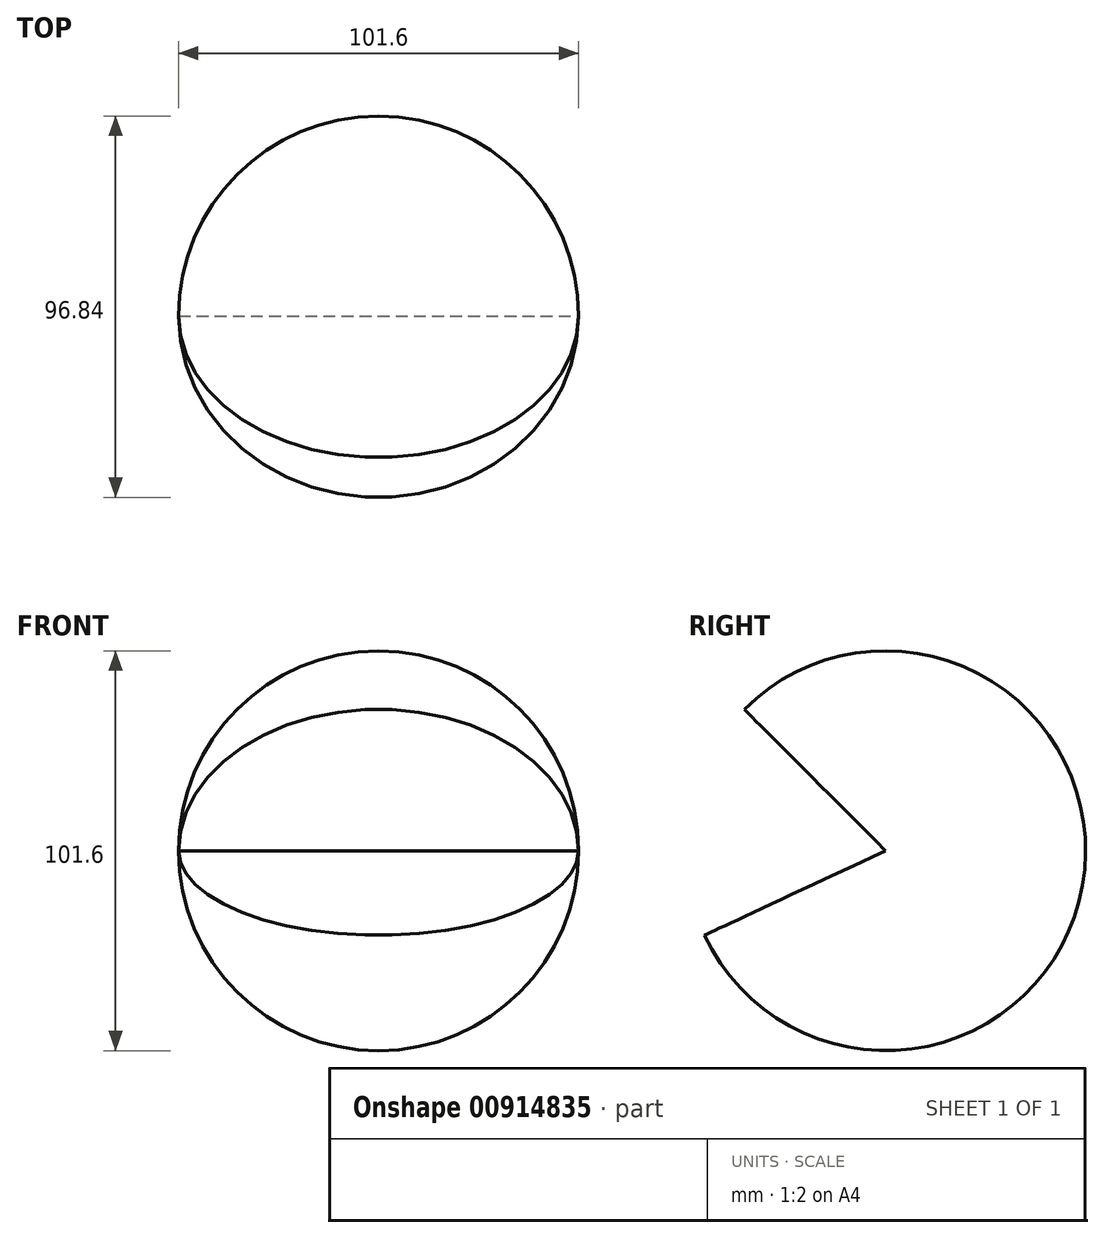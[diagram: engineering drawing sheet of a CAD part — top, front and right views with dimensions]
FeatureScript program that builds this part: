
annotation { "Feature Type Name" : "Feature", "Feature Type Description" : "" }
export const myFeature = defineFeature(function(context is Context, id is Id, definition is map)
    precondition{}
    {
        {
            var Q0;
            Q0=qCreatedBy(makeId("Top.planeOp"),FACE);
            var sketch = newSketch(context, id + "F0", { "sketchPlane" : qUnion([Q0])});
            skLineSegment(sketch, "E0.bottom", {"start": v(-0.24, 50.8) * mm, "end": v(-0.24, 50.8) * mm});
            skLineSegment(sketch, "E0.top", {"start": v(-51.04, 0) * mm, "end": v(50.56, 0) * mm});
            skLineSegment(sketch, "E0.left", {"start": v(-51.04, 0) * mm, "end": v(-51.04, 0) * mm});
            skLineSegment(sketch, "E0.right", {"start": v(50.56, 0) * mm, "end": v(50.56, 0) * mm});
            skLineSegment(sketch, "E1", {"start": v(0, 50.8) * mm, "end": v(0, 0) * mm, "construction": true});
            skPoint(sketch, "E2.visualSharp", {"position": v(-51.04, 50.8) * mm});
            skArc(sketch, "E2.filletArc", {"start": v(-0.24, 50.8) * mm, "mid": v(-36.16, 35.92) * mm, "end": v(-51.04, 0) * mm});
            skPoint(sketch, "E3.visualSharp", {"position": v(50.56, 50.8) * mm});
            skArc(sketch, "E3.filletArc", {"start": v(50.56, 0) * mm, "mid": v(35.68, 35.92) * mm, "end": v(-0.24, 50.8) * mm});
            skSolve(sketch);
        }
        {
            var Q0;
            Q0=makeQuery(id+"F0.imprint","IMPRINT",FACE,{"disambiguationData":[TD([[makeQuery(id+"F0.imprint","IMPRINT",EDGE,{"derivedFrom":sQuery(id+"F0.wireOp",EDGE,"E0.top")}),1.0]])]});
            var Q1;
            Q1=sQuery(id+"F0.wireOp",EDGE,"E0.top");
            revolve(context, id + "F1", {"surfaceOperationType" : NewSurfaceOperationType.NEW, "entities" : qUnion([Q0]), "axis" : qUnion([Q1]), "revolveType" : RevolveType.TWO_DIRECTIONS, "angle" : 135 * degree, "angleBack" : 205 * degree});
        }
    });
